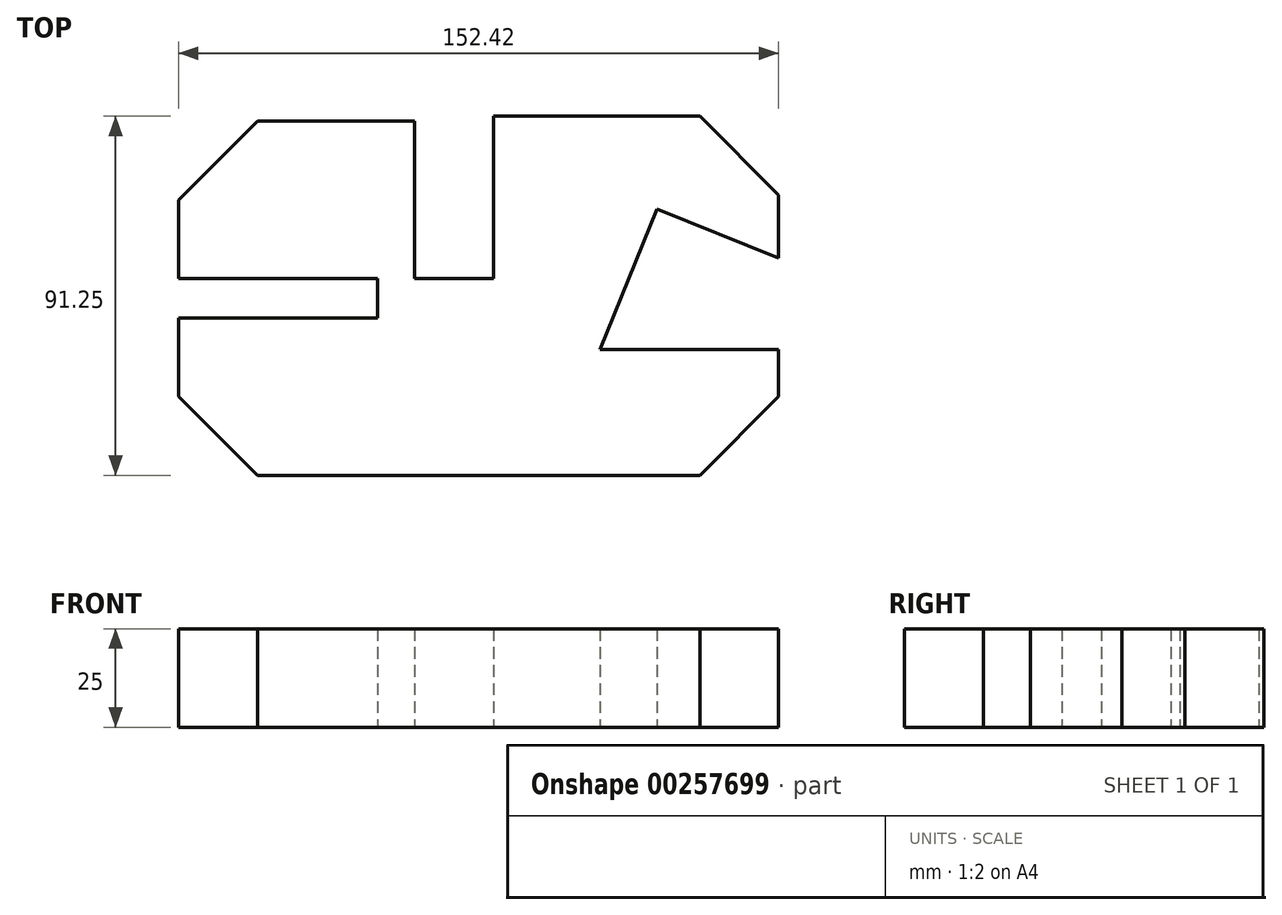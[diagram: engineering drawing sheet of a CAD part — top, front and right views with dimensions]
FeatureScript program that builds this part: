
annotation { "Feature Type Name" : "Feature", "Feature Type Description" : "" }
export const myFeature = defineFeature(function(context is Context, id is Id, definition is map)
    precondition{}
    {
        {
            var Q0;
            Q0=qCreatedBy(makeId("Top.planeOp"),FACE);
            var sketch = newSketch(context, id + "F0", { "sketchPlane" : qUnion([Q0])});
            skLineSegment(sketch, "E0", {"start": v(-60, -46.66) * mm, "end": v(52.4, -46.66) * mm});
            skLineSegment(sketch, "E1", {"start": v(52.4, -46.66) * mm, "end": v(72.4, -26.64) * mm});
            skLineSegment(sketch, "E2", {"start": v(72.4, -26.64) * mm, "end": v(72.4, -14.64) * mm});
            skLineSegment(sketch, "E3", {"start": v(72.4, -14.64) * mm, "end": v(27.1, -14.64) * mm});
            skLineSegment(sketch, "E4", {"start": v(27.1, -14.64) * mm, "end": v(41.53, 21.05) * mm});
            skLineSegment(sketch, "E5", {"start": v(41.53, 21.05) * mm, "end": v(72.41, 8.58) * mm});
            skLineSegment(sketch, "E6", {"start": v(72.41, 8.58) * mm, "end": v(72.41, 24.58) * mm});
            skLineSegment(sketch, "E7", {"start": v(72.41, 24.58) * mm, "end": v(52.4, 44.59) * mm});
            skLineSegment(sketch, "E8", {"start": v(52.4, 44.59) * mm, "end": v(0, 44.59) * mm});
            skLineSegment(sketch, "E9", {"start": v(0, 44.59) * mm, "end": v(0, 3.35) * mm});
            skLineSegment(sketch, "E10", {"start": v(0, 3.35) * mm, "end": v(-20, 3.35) * mm});
            skLineSegment(sketch, "E11", {"start": v(-20, 3.35) * mm, "end": v(-20, 43.36) * mm});
            skLineSegment(sketch, "E12", {"start": v(-20, 43.36) * mm, "end": v(-60, 43.36) * mm});
            skLineSegment(sketch, "E13", {"start": v(-60, 43.36) * mm, "end": v(-80.01, 23.35) * mm});
            skLineSegment(sketch, "E14", {"start": v(-80.01, 23.35) * mm, "end": v(-80.01, 3.35) * mm});
            skLineSegment(sketch, "E15", {"start": v(-80.01, 3.35) * mm, "end": v(-29.51, 3.35) * mm});
            skLineSegment(sketch, "E16", {"start": v(-29.51, 3.35) * mm, "end": v(-29.51, -6.65) * mm});
            skLineSegment(sketch, "E17", {"start": v(-29.51, -6.65) * mm, "end": v(-80.01, -6.65) * mm});
            skLineSegment(sketch, "E18", {"start": v(-80.01, -6.65) * mm, "end": v(-80.01, -26.65) * mm});
            skLineSegment(sketch, "E19", {"start": v(-80.01, -26.65) * mm, "end": v(-60, -46.66) * mm});
            skSolve(sketch);
        }
        {
            var Q0;
            Q0=makeQuery(id+"F0.imprint","IMPRINT",FACE,{"disambiguationData":[TD([[makeQuery(id+"F0.imprint","IMPRINT",EDGE,{"derivedFrom":sQuery(id+"F0.wireOp",EDGE,"E0")}),1.0]])]});
            extrude(context, id + "F1", {"entities" : qUnion([Q0]), "depth" : 25 * mm});
        }
    });
